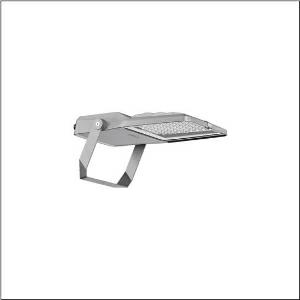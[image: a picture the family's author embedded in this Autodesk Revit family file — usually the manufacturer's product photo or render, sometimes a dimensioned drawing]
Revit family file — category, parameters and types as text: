
# Revit family: floodlight_fl_21_iq_mini___pl64_5xa7772b1e1a_f8ab
name_source: partatom
category: Lighting Fixtures
units: mm (PartAtom-declared; Revit-internal decimal feet)

## family parameters
Cut with Voids When Loaded = No
Host = Face
Light Source = No
Part Type = Normal
Room Calculation Point = No
Round Connector Dimension = Use Diameter
Shared = No

## types (1)
- --- (1 x LED, 4990 lm, 45.5 W, 2200K)
    Apparent Load = 46 VA
    CIE Flux Codes = 28 80 98 100 100
    Color Rendering = 70
    Color Temperature = 2200K
    Default Elevation = 1800 mm
    Description = Floodlight FL 21 iQ mini, floodlight, primary light control with lens, of PMMA, primary optical cover: protective disc, of toughened safety glass, transparent, light distribution: PL64, light emission: direct distribution, installation type: surface-mounted, lamps: LED, High Power LED, rated values: 4.990lm | 45,5W | 109,7lm/W (begin service life); end service life: 4.990lm | 48W; at 50% lumin. flux: 2.495lm | 21,4W | 116,6lm/W, colour temperature: 2200K, colour rendering: CRI > 70, light colour: 722, light setting 1 begin service life: 100% | 4.990lm | 45,5W | 109,7lm/W | 2.200K, light setting 1 end service life: 48W, further light settings possible, control: Street-Remote, Auto-Match, Temp-Guard, Night-Set, Smart-Wire, Desk-Remote (wireless, voltage-free reading and setting of iQ features in the workshop via application-optimized NFC function/RFID function), optimised constant luminous flux control (CLO 2.0), pre-setting: linear dimming characteristic, with terminal, 6-pole, mains connection: 220..240V, AC, 50/60Hz, luminaire housing, of diecast aluminium, powder-coated, SITECO metallic grey (DB 702S), corrosivity category C5 mid according to DIN EN ISO 12944suitable for swimming poolschlorine-resistant, sealing non-destructively replaceable, mounting bracket, of steel, galvanised, powder-coated, SITECO metallic grey (DB 702S), protection rating (complete): IP66, insulation class (complete): insulation class II (safety insulation), certification: CE, ENEC, VDE, protection symbol: D, impact resistance: IK08, permissible operating ambient temperature: -40..+40°C, permissible operating ambient temperature for outdoor applications: -40..+50°C, standard: DIN EN 12944, LABS conformity tested according to VDMA 24364:2018-05, packaging unit: 1 piece

Light Distribution: PL64
    Height = 70 mm
    Lamp = 1 x LED
    Lamp Light Flux = 4990 lm
    Lamp Power = 45.5 W
    Lamp count = 1
    Length = 485 mm
    Luminous efficacy = 110 lm/W
    Manufacturer = Siteco
    ModVariant = No
    Model = 5XA7772B1E1A
    Number of Poles = 1
    OnlyDefault = Yes
    Power Factor = 1
    Product Name = Floodlight FL 21 iQ mini | PL64
    Product group = floodlight | pylon annexe
    ProductGroupID = 6201
    Protection Class = Protection class II
    Protection Degree = IP 66
    RLX_Detail_Level = 1
    RLX_Emergency_Light_Flux = 0 lm
    RLX_Emergency_Type = 0
    RLX_Emergency_Type_DB = No
    RlxData = <blob elided: 96449 chars, md5=33ab378b>
    Socket = socket
    Standby Power = 0 W
    System Light Flux = 4990 lm
    System Power = 46 W
    Type Comments = factory setting: luminous flux: 100 % | dim-lin: 254 | 463 mA
    Type Image = l_1006845.jpg
    URL = http://relux.com
    VarID = @adj_166487
    Voltage = 0 V
    Weight = 0.00 kg
    Width = 337 mm

## geometry (parser evidence)
native form markers: Blend x4, Sweep x12
no freeform markers — native parametric forms only
